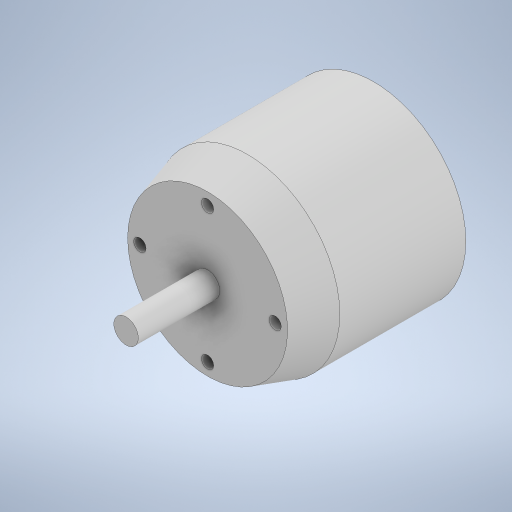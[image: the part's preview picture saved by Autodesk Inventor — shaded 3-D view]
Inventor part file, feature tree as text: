
AUTODESK INVENTOR PART (.ipt)
format: ipt  version: 2023 (Build 270158000, 158)  size: 253,440 bytes
history: native  units: mm
features: sketch x6, extrude x3, plane x1, loft x1, other x1
ambient origin geometry x8: Origin, YZ Plane, XZ Plane, XY Plane, X Axis, Y Axis, Z Axis, Center Point
bodies: Solid1 (feature_tree)
feature tree (12):
  extrude  "Extrusion1"  Depth=41.0mm TaperAngle=0.0deg
  plane  "Work Plane1"
  loft  "Loft1"
  sketch  "Sketch4"  dims[d5=0.0mm d6=90.0deg d7=0.0mm d8=90.0deg]
  extrude  "Extrusion2"  TaperAngle=0.0deg  [1 undecoded]
  sketch  "Sketch6"  dims[d13=5.0mm d14=0.0mm]
  extrude  "Extrusion3"  Depth=4.0mm
  sketch  "Sketch1"  dims[d0=60.0mm d1=41.0mm d2=0.0mm]
  sketch  "Sketch2"  dims[d3=13.0mm d4=52.0mm]
  other  "Edges1"
  sketch  "Sketch5"  dims[d11=4.0mm d12=44.0mm]
  sketch  "Sketch7"  dims[d16=8.0mm d17=26.5mm d18=58.0mm d19=0.0mm d20=0.0mm]
note: 1 required parameter value undecoded (feature->parameter linkage not recoverable at this tier; creation-order binding heuristic only, values carry confidence <= 0.55)
